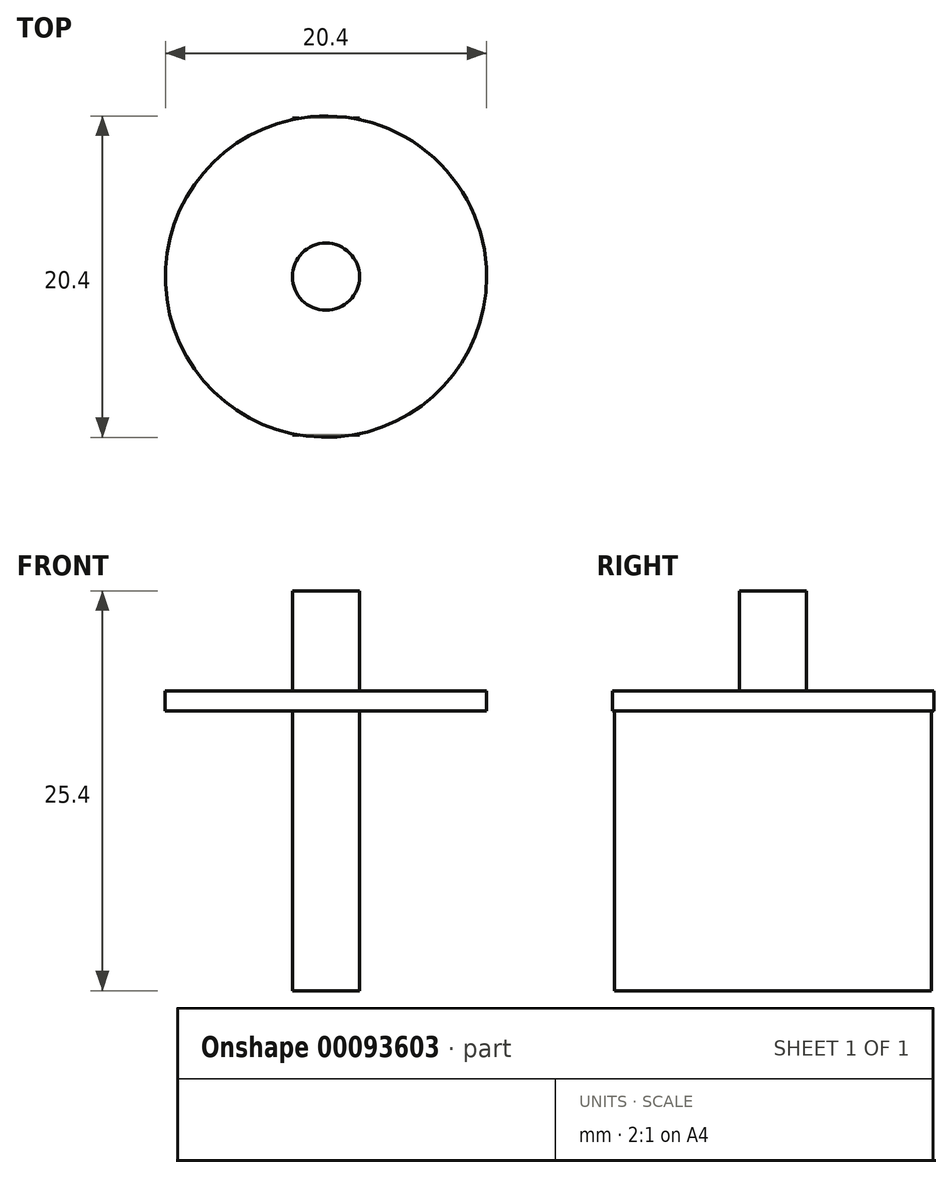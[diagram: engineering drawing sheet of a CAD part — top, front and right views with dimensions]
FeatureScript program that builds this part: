
annotation { "Feature Type Name" : "Feature", "Feature Type Description" : "" }
export const myFeature = defineFeature(function(context is Context, id is Id, definition is map)
    precondition{}
    {
        {
            var Q0;
            Q0=qCreatedBy(makeId("Top.planeOp"),FACE);
            var sketch = newSketch(context, id + "F0", { "sketchPlane" : qUnion([Q0])});
            skPoint(sketch, "E0", {"position": v(0, 0) * mm});
            skLineSegment(sketch, "E1.bottom", {"start": v(2.12, 10.06) * mm, "end": v(-2.12, 10.06) * mm});
            skLineSegment(sketch, "E1.top", {"start": v(2.12, -10.06) * mm, "end": v(-2.12, -10.06) * mm});
            skLineSegment(sketch, "E1.left", {"start": v(2.12, 10.06) * mm, "end": v(2.12, -10.06) * mm});
            skLineSegment(sketch, "E1.right", {"start": v(-2.12, 10.06) * mm, "end": v(-2.12, -10.06) * mm});
            skPoint(sketch, "E2", {"position": v(2.12, 10.06) * mm});
            skPoint(sketch, "E3", {"position": v(-2.12, 10.06) * mm});
            skPoint(sketch, "E4", {"position": v(2.12, -10.06) * mm});
            skPoint(sketch, "E5", {"position": v(-2.12, -10.06) * mm});
            skSolve(sketch);
        }
        {
            var Q0;
            Q0=qCreatedBy(makeId("Top.planeOp"),FACE);
            cPlane(context, id + "F6", {"entities" : qUnion([Q0]), "cplaneType" : CPlaneType.OFFSET, "offset" : 17.78 * mm, "width" : 152.4 * mm, "height" : 152.4 * mm});
        }
        {
            var Q0;
            Q0=qCreatedBy(id+"F6.planeOp",FACE);
            var sketch = newSketch(context, id + "F1", { "sketchPlane" : qUnion([Q0])});
            skPoint(sketch, "E6", {"position": v(0, 0) * mm});
            skPoint(sketch, "E7", {"position": v(2.13, 0) * mm});
            skCircle(sketch, "E8", {"center": v(0, 0) * mm, "radius": 2.13 * mm});
            skCircle(sketch, "E9", {"center": v(0, 0) * mm, "radius": 10.2 * mm});
            skSolve(sketch);
        }
        {
            var Q0;
            Q0=makeQuery(id+"F0.imprint","IMPRINT",FACE,{"disambiguationData":[TD([[makeQuery(id+"F0.imprint","IMPRINT",EDGE,{"derivedFrom":sQuery(id+"F0.wireOp",EDGE,"E1.bottom")}),1.0]])]});
            extrude(context, id + "F7", {"entities" : qUnion([Q0]), "depth" : 17.78 * mm});
        }
        {
            var Q0;
            Q0=makeQuery(id+"F1.imprint","IMPRINT",FACE,{"disambiguationData":[TD([[makeQuery(id+"F1.imprint","IMPRINT",EDGE,{"derivedFrom":sQuery(id+"F1.wireOp",EDGE,"E8")}),1.0]])]});
            extrude(context, id + "F2", {"entities" : qUnion([Q0]), "operationType" : NewBodyOperationType.ADD, "depth" : 7.62 * mm});
        }
        {
            var Q0;
            Q0=makeQuery(id+"F1.imprint","IMPRINT",FACE,{"disambiguationData":[TD([[makeQuery(id+"F1.imprint","IMPRINT",EDGE,{"derivedFrom":sQuery(id+"F1.wireOp",EDGE,"E8")}),-1.0]])]});
            extrude(context, id + "F3", {"entities" : qUnion([Q0]), "operationType" : NewBodyOperationType.ADD, "depth" : 1.27 * mm});
        }
        {
            var Q0;
            Q0=qCreatedBy(id+"F6.planeOp",FACE);
            cPlane(context, id + "F4", {"entities" : qUnion([Q0]), "cplaneType" : CPlaneType.OFFSET, "offset" : 7.62 * mm, "width" : 152.4 * mm, "height" : 152.4 * mm});
        }
    });
